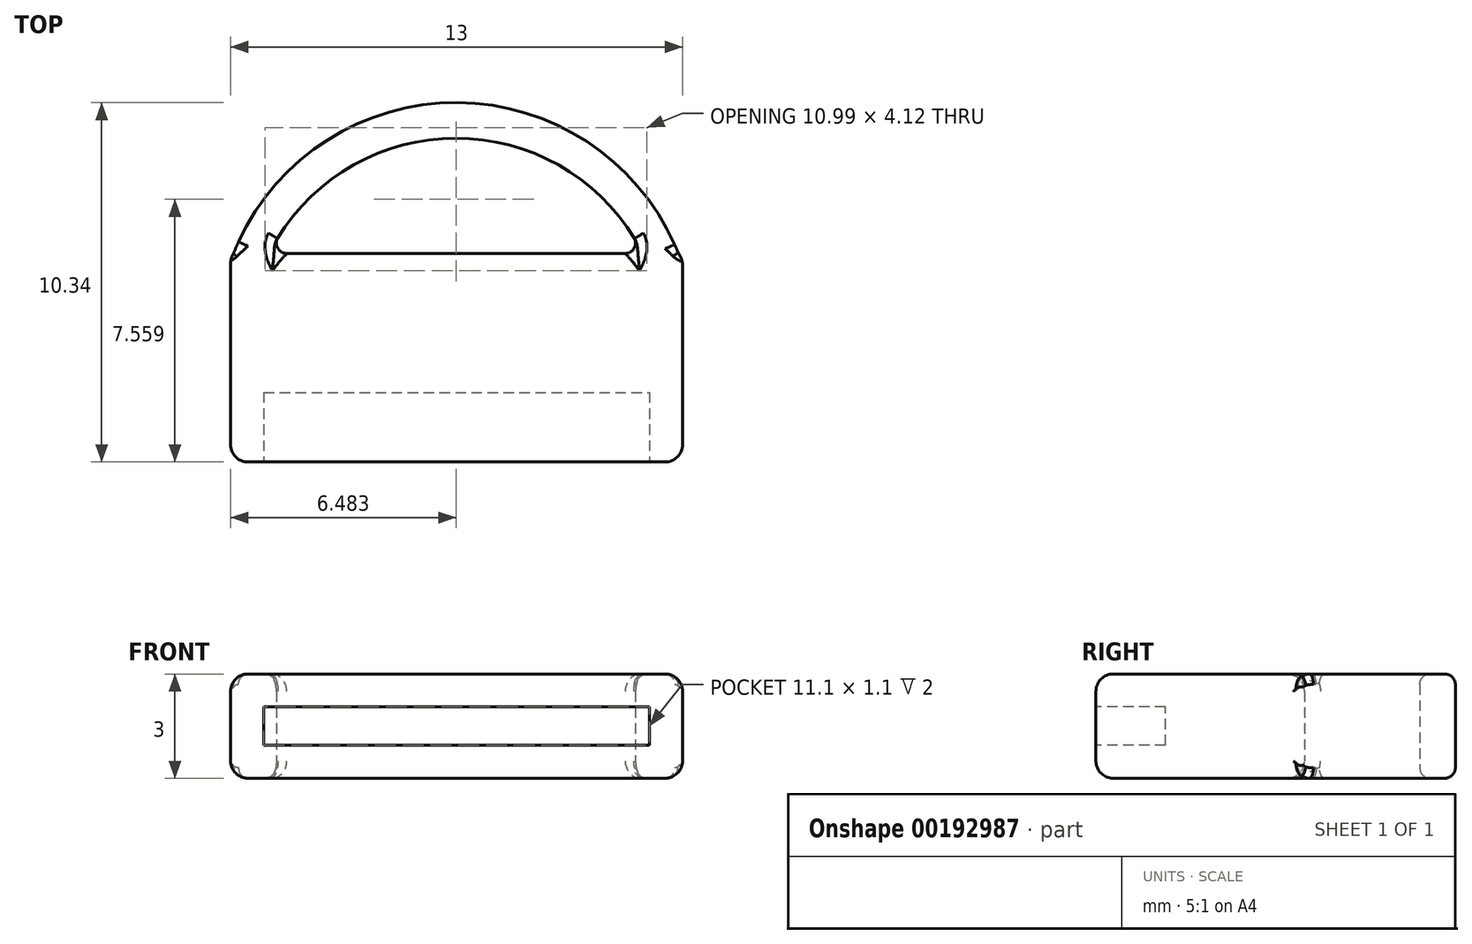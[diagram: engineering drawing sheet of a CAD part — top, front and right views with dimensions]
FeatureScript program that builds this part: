
annotation { "Feature Type Name" : "Feature", "Feature Type Description" : "" }
export const myFeature = defineFeature(function(context is Context, id is Id, definition is map)
    precondition{}
    {
        {
            var Q0;
            Q0=qCreatedBy(makeId("Front.planeOp"),FACE);
            var sketch = newSketch(context, id + "F0", { "sketchPlane" : qUnion([Q0])});
            skLineSegment(sketch, "E0.bottom", {"start": v(-6.5, -1.5) * mm, "end": v(6.5, -1.5) * mm});
            skLineSegment(sketch, "E0.top", {"start": v(-6.5, 1.5) * mm, "end": v(6.5, 1.5) * mm});
            skLineSegment(sketch, "E0.left", {"start": v(-6.5, -1.5) * mm, "end": v(-6.5, 1.5) * mm});
            skLineSegment(sketch, "E0.right", {"start": v(6.5, -1.5) * mm, "end": v(6.5, 1.5) * mm});
            skPoint(sketch, "E0.middle", {"position": v(0, 0) * mm});
            skSolve(sketch);
        }
        {
            var Q0;
            Q0=makeQuery(id+"F0.imprint","IMPRINT",FACE,{"disambiguationData":[TD([[makeQuery(id+"F0.imprint","IMPRINT",EDGE,{"derivedFrom":sQuery(id+"F0.wireOp",EDGE,"E0.bottom")}),1.0]])]});
            extrude(context, id + "F1", {"entities" : qUnion([Q0]), "depth" : 6 * mm});
        }
        {
            var Q0;
            Q0=makeQuery(id+"F1.opExtrude","CAP_FACE",FACE,{"disambiguationData":[OSD([sQuery(id+"F0.wireOp",EDGE,"E0.bottom"),sQuery(id+"F0.wireOp",EDGE,"E0.top"),sQuery(id+"F0.wireOp",EDGE,"E0.left"),sQuery(id+"F0.wireOp",EDGE,"E0.right")])],"isStart":false});
            var sketch = newSketch(context, id + "F2", { "sketchPlane" : qUnion([Q0])});
            skLineSegment(sketch, "E1.bottom", {"start": v(-5.55, -0.55) * mm, "end": v(5.55, -0.55) * mm});
            skLineSegment(sketch, "E1.top", {"start": v(-5.55, 0.55) * mm, "end": v(5.55, 0.55) * mm});
            skLineSegment(sketch, "E1.left", {"start": v(-5.55, -0.55) * mm, "end": v(-5.55, 0.55) * mm});
            skLineSegment(sketch, "E1.right", {"start": v(5.55, -0.55) * mm, "end": v(5.55, 0.55) * mm});
            skPoint(sketch, "E1.middle", {"position": v(0, 0) * mm});
            skSolve(sketch);
        }
        {
            var Q0;
            Q0=qCreatedBy(makeId("Top.planeOp"),FACE);
            var sketch = newSketch(context, id + "F3", { "sketchPlane" : qUnion([Q0])});
            skPoint(sketch, "E2", {"position": v(-6.42, 0) * mm});
            skPoint(sketch, "E3", {"position": v(6.38, 0) * mm});
            skPoint(sketch, "E4", {"position": v(0, 4.34) * mm});
            skArc(sketch, "E5", {"start": v(6.38, 0) * mm, "mid": v(-0.02, 4.34) * mm, "end": v(-6.42, 0) * mm});
            skPoint(sketch, "E6", {"position": v(-5.4, 0) * mm});
            skPoint(sketch, "E7", {"position": v(5.36, 0) * mm});
            skPoint(sketch, "E8", {"position": v(0, 3.32) * mm});
            skArc(sketch, "E9", {"start": v(5.36, 0) * mm, "mid": v(-0.02, 3.32) * mm, "end": v(-5.4, 0) * mm});
            skLineSegment(sketch, "E10", {"start": v(-6.42, 0) * mm, "end": v(-5.4, 0) * mm});
            skLineSegment(sketch, "E11", {"start": v(5.36, 0) * mm, "end": v(6.38, 0) * mm});
            skSolve(sketch);
        }
        {
            var Q0;
            Q0=makeQuery(id+"F3.imprint","IMPRINT",FACE,{"disambiguationData":[TD([[makeQuery(id+"F3.imprint","IMPRINT",EDGE,{"derivedFrom":sQuery(id+"F3.wireOp",EDGE,"E5")}),1.0]])]});
            extrude(context, id + "F4", {"entities" : qUnion([Q0]), "operationType" : NewBodyOperationType.ADD, "depth" : 1.5 * mm, "hasSecondDirection" : true, "secondDirectionOppositeDirection" : true, "secondDirectionDepth" : 1.5 * mm});
        }
        {
            var Q0;
            Q0=makeQuery(id+"F1.opExtrude","SWEPT_EDGE",EDGE,{"disambiguationData":[OSD([sQuery(id+"F0.wireOp",EDGE,"E0.bottom"),sQuery(id+"F0.wireOp",EDGE,"E0.left")])]});
            var Q1;
            Q1=makeQuery(id+"F1.opExtrude","SWEPT_FACE",FACE,{"disambiguationData":[OSD([sQuery(id+"F0.wireOp",EDGE,"E0.right")])]});
            var Q2;
            Q2=makeQuery(id+"F1.opExtrude","CAP_FACE",FACE,{"disambiguationData":[OSD([sQuery(id+"F0.wireOp",EDGE,"E0.bottom"),sQuery(id+"F0.wireOp",EDGE,"E0.top"),sQuery(id+"F0.wireOp",EDGE,"E0.left"),sQuery(id+"F0.wireOp",EDGE,"E0.right")])],"isStart":false});
            var Q3;
            Q3=makeQuery(id+"F1.opExtrude","SWEPT_FACE",FACE,{"disambiguationData":[OSD([sQuery(id+"F0.wireOp",EDGE,"E0.left")])]});
            var Q4;
            {var subQ0=sQuery(id+"F0.wireOp",EDGE,"E0.top");var subQ1=sQuery(id+"F3.wireOp",EDGE,"E9");Q4=makeQuery(id+"F4.boolean.opBoolean","SPLIT",EDGE,{"disambiguationData":[TD([makeQuery(id+"F4.opExtrude","SWEPT_FACE",FACE,{"disambiguationData":[OSD([subQ1])]})])],"derivedFrom":makeQuery(id+"F1.opExtrude","CAP_EDGE",EDGE,{"disambiguationData":[OSD([subQ0])],"isStart":true})});}
            var Q5;
            {var subQ0=sQuery(id+"F0.wireOp",EDGE,"E0.bottom");var subQ1=sQuery(id+"F3.wireOp",EDGE,"E9");Q5=makeQuery(id+"F4.boolean.opBoolean","SPLIT",EDGE,{"disambiguationData":[TD([makeQuery(id+"F4.opExtrude","SWEPT_FACE",FACE,{"disambiguationData":[OSD([subQ1])]})])],"derivedFrom":makeQuery(id+"F1.opExtrude","CAP_EDGE",EDGE,{"disambiguationData":[OSD([subQ0])],"isStart":true})});}
            fillet(context, id + "F5", {"entities" : qUnion([Q0, Q1, Q2, Q3, Q4, Q5]), "radius" : 0.5 * mm, "tangentPropagation" : true, "allowEdgeOverflow" : false});
        }
        {
            var Q0;
            Q0=makeQuery(id+"F2.imprint","IMPRINT",FACE,{"disambiguationData":[TD([[makeQuery(id+"F2.imprint","IMPRINT",EDGE,{"derivedFrom":sQuery(id+"F2.wireOp",EDGE,"E1.bottom")}),1.0]])]});
            extrude(context, id + "F6", {"entities" : qUnion([Q0]), "operationType" : NewBodyOperationType.REMOVE, "oppositeDirection" : true, "depth" : 2 * mm});
        }
        {
            var Q0;
            Q0=makeQuery(id+"F4.opExtrude","SWEPT_FACE",FACE,{"disambiguationData":[OSD([sQuery(id+"F3.wireOp",EDGE,"E9")])]});
            var Q1;
            Q1=makeQuery(id+"F4.opExtrude","SWEPT_FACE",FACE,{"disambiguationData":[OSD([sQuery(id+"F3.wireOp",EDGE,"E5")])]});
            fillet(context, id + "F7", {"entities" : qUnion([Q0, Q1]), "radius" : 0.3 * mm, "allowEdgeOverflow" : false});
        }
    });
